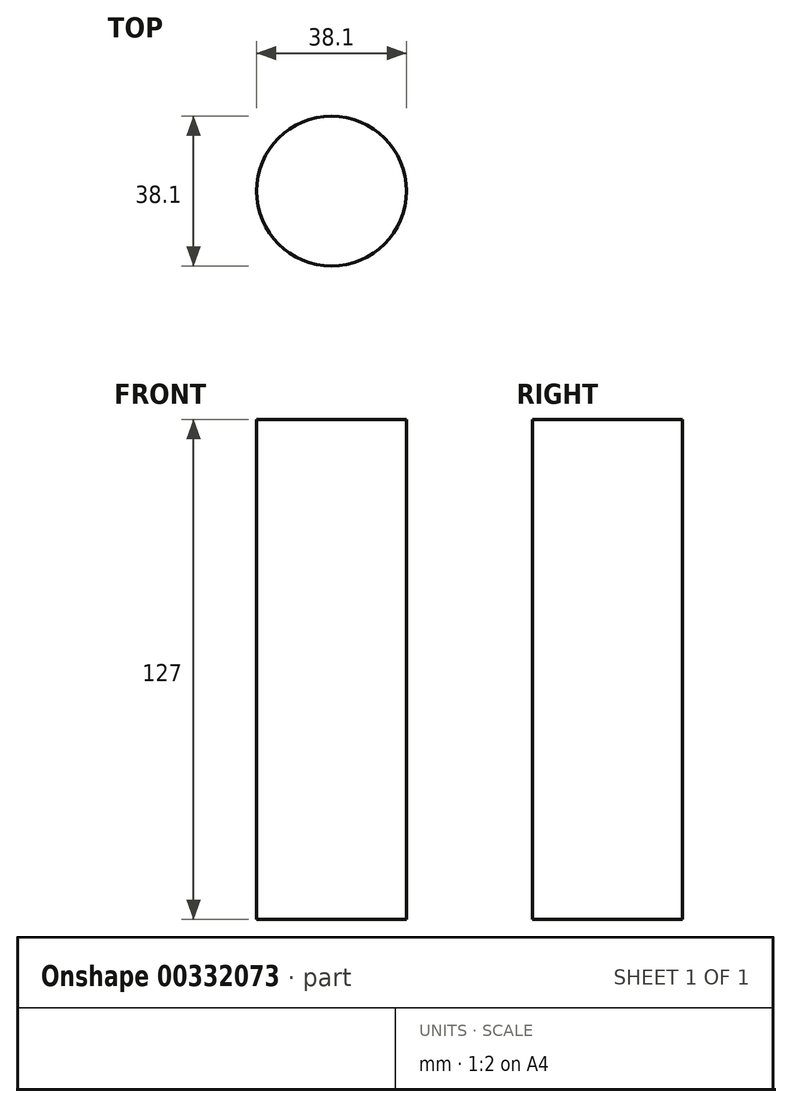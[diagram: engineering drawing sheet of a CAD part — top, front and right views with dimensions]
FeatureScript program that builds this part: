
annotation { "Feature Type Name" : "Feature", "Feature Type Description" : "" }
export const myFeature = defineFeature(function(context is Context, id is Id, definition is map)
    precondition{}
    {
        {
            var Q0;
            Q0=qCreatedBy(makeId("Top.planeOp"),FACE);
            cPlane(context, id + "F0", {"entities" : qUnion([Q0]), "cplaneType" : CPlaneType.OFFSET, "offset" : 127 * mm, "width" : 152.4 * mm, "height" : 152.4 * mm});
        }
        {
            var Q0;
            Q0=qCreatedBy(makeId("Top.planeOp"),FACE);
            var sketch = newSketch(context, id + "F1", { "sketchPlane" : qUnion([Q0])});
            skCircle(sketch, "E0", {"center": v(0, 0) * mm, "radius": 19.05 * mm});
            skSolve(sketch);
        }
        {
            var Q0;
            Q0=qCreatedBy(id+"F0.planeOp",FACE);
            var sketch = newSketch(context, id + "F2", { "sketchPlane" : qUnion([Q0])});
            skCircle(sketch, "E1", {"center": v(0, 0) * mm, "radius": 19.05 * mm});
            skSolve(sketch);
        }
        {
            var Q0;
            Q0=makeQuery(id+"F2.imprint","IMPRINT",FACE,{"disambiguationData":[TD([[makeQuery(id+"F2.imprint","IMPRINT",EDGE,{"derivedFrom":sQuery(id+"F2.wireOp",EDGE,"E1")}),1.0]])]});
            var Q1;
            Q1=makeQuery(id+"F1.imprint","IMPRINT",FACE,{"disambiguationData":[TD([[makeQuery(id+"F1.imprint","IMPRINT",EDGE,{"derivedFrom":sQuery(id+"F1.wireOp",EDGE,"E0")}),1.0]])]});
            loft(context, id + "F3", {"sheetProfilesArray" : [{ "sheetProfileEntities" : qUnion([Q0]) }, { "sheetProfileEntities" : qUnion([Q1]) }]});
        }
    });
